FCSTD DOCUMENT  (FreeCAD 0.22R37100 (Git))
Label: composit_stand3_sleeve_model
License: All rights reserved
LicenseURL: http://en.wikipedia.org/wiki/All_rights_reserved
objects: App::Link×2, App::DocumentObjectGroup×1, PartDesign::CoordinateSystem×1, App::Part×1
note: 1 computed .brp shape members not serialized (recipe doc carries the construction recipe); baked Part::Feature solids carry a one-line shape summary decoded from their .brp
EXTERNAL_REF file=composit_stand3_sleeve_outer_model.FCStd obj=Local_CS
EXTERNAL_REF file=composit_stand3_sleeve_outer_model.FCStd obj=Body
EXTERNAL_REF file=composit_stand3_sleeve_outer_model.FCStd obj=Local_CS001
EXTERNAL_REF file=composit_stand3_sleeve_inner_model.FCStd obj=Local_CS
EXTERNAL_REF file=composit_stand3_sleeve_inner_model.FCStd obj=Body

FEATURE [App::DocumentObjectGroup] Parts
FEATURE [PartDesign::CoordinateSystem] LCS_Origin
  AttacherType = Attacher::AttachEngine3D
FEATURE [App::Link] sleeve_outer
  AttachedBy = #Local_CS
  AttachedTo = Parent Assembly#LCS_Origin
  LinkedObject = -> <external composit_stand3_sleeve_outer_model.FCStd>#Body
  SolverId = Asm4EE
  expr: Placement = LCS_Origin.Placement * AttachmentOffset * Unnamed#Local_CS.Placement ^ -1
FEATURE [App::Link] sleeve_inner
  AttachedBy = #Local_CS
  AttachedTo = sleeve_outer#Local_CS001
  LinkPlacement = pos=(0,2.3e-15,58.6519) rot=(1,0,0;3.14159rad)
  LinkedObject = -> <external composit_stand3_sleeve_inner_model.FCStd>#Body
  Placement = pos=(0,2.3e-15,58.6519) rot=(1,0,0;3.14159rad)
  SolverId = Asm4EE
  expr: Placement = sleeve_outer.Placement * Unnamed#Local_CS001.Placement * AttachmentOffset * composit_stand3_sleeve_inner_model#Local_CS.Placement ^ -1
FEATURE [App::Part] Assembly
  AssemblyType = Part::Link
  Group = -> [LCS_Origin,sleeve_outer,sleeve_inner]
  Origin = -> Origin
  Type = Assembly

RESOLVED EXTERNAL PARTS (link-assembly join: the EXTERNAL_REF files above that resolve inside this repo's crawl, each included once):
---- part composit_stand3_sleeve_inner_model.FCStd = doc fcstd_342576fd2858 ----
FCSTD DOCUMENT  (FreeCAD 1.1R38827 (Git))
Label: composit_stand3_sleeve_inner_model
License: All rights reserved
LicenseURL: http://en.wikipedia.org/wiki/All_rights_reserved
objects: PartDesign::SubShapeBinder×2, PartDesign::Body×2, PartDesign::Revolution×1, PartDesign::CoordinateSystem×1, Part::Feature×1, App::Link×1, Part::Cylinder×1, Part::FeaturePython×1, Part::MultiFuse×1, PartDesign::Boolean×1
note: 14 computed .brp shape members not serialized (recipe doc carries the construction recipe); baked Part::Feature solids carry a one-line shape summary decoded from their .brp
EXTERNAL_REF file=composit_stand3_sleeve_inner_main.FCStd obj=Sketch
EXTERNAL_REF file=composit_stand3_sleeve_inner_main.FCStd obj=PolarArray

FEATURE [PartDesign::SubShapeBinder] Binder
  BindCopyOnChange = 0
  BindMode = 0
  ClaimChildren = true
  Fuse = false
  MakeFace = true
  OffsetFill = false
  OffsetIntersection = false
  OffsetJoinType = 0
  OffsetOpenResult = false
  PartialLoad = false
  Placement = pos=(0,0,0) rot=(1,0,0;1.5708rad)
  Relative = false
  Support = -> [<external composit_stand3_sleeve_inner_main.FCStd>#Sketch]
  _Version = 2
FEATURE [PartDesign::SubShapeBinder] Binder001
  BindCopyOnChange = 0
  BindMode = 0
  ClaimChildren = true
  Context = -> Body [Binder001.]
  Fuse = false
  MakeFace = true
  OffsetFill = false
  OffsetIntersection = false
  OffsetJoinType = 0
  OffsetOpenResult = false
  PartialLoad = false
  Placement = pos=(0,0,0) rot=(1,0,0;1.5708rad)
  Relative = false
  Support = -> [Binder]
  _Version = 2
FEATURE [PartDesign::Revolution] Revolution
  Angle = 360
  Angle2 = 60
  Axis = (1e-16,1e-16,1)
  Base = (0,0,0)
  Placement = pos=(0,0,0) rot=(1,0,0;1.5708rad)
  Profile = -> Binder001 [Face1]
  ReferenceAxis = -> Z_Axis
  Reversed = true
  Suppressed = false
  Type = 0
FEATURE [PartDesign::CoordinateSystem] Local_CS
  AttacherType = Attacher::AttachEngine3D
  AttachmentOffset = pos=(0,0,8) rot=(0,0,1;0rad)
  AttachmentSupport = -> [XY_Plane]
  MapMode = 5
  Placement = pos=(0,0,8) rot=(0,0,1;0rad)
  expr: .AttachmentOffset.Base.z = <<composit_stand3_sleeve_inner_main>>#<<sleeve_inner_base_sketch>>.Constraints.base_height
FEATURE [Part::Feature] Body169  label="sleeve_inner002"
  shape: bbox 66 x 66 x 79 mm, 9 faces (baked)
FEATURE [App::Link] Link  label="PolarArray"
  LinkTransform = true
  LinkedObject = -> <external composit_stand3_sleeve_inner_main.FCStd>#PolarArray
FEATURE [Part::Cylinder] Cylinder
  Angle = 360
  AttacherType = Attacher::AttachEngine3D
  FirstAngle = 0
  Height = 20
  Placement = pos=(0,0,0) rot=(1,0,0;3.14159rad)
  Radius = 2
  SecondAngle = 0
FEATURE [Part::FeaturePython] Populate  label="Populate PolarArray with Cylinder"  # WARN: FeaturePython — macro-defined, semantics opaque (R4)
  Copying = 0
  ExposePlacement = false
  MarkerShape = 1
  MarkerSize = 0
  NumElements = 0
  Object = -> Cylinder
  OutputCompounding = 1
  PlacementsTo = -> Link
  Referencing = 0
  Type = lattice2PopulateCopies.LatticePopulateCopies
  isLattice = 0
FEATURE [PartDesign::Body] Body170  label="Body"
  AllowCompound = false
  Origin = -> Origin001
FEATURE [Part::MultiFuse] Fusion
  Shapes = -> [Populate]
FEATURE [PartDesign::Boolean] Boolean
  BaseFeature = -> Revolution
  Group = -> [Fusion]
  Suppressed = false
  Type = 1
  UsePlacement = true
FEATURE [PartDesign::Body] Body  label="sleeve_inner"
  AllowCompound = false
  Group = -> [Binder001,Revolution,Local_CS,Boolean]
  Origin = -> Origin
  Tip = -> Boolean
---- part composit_stand3_sleeve_outer_model.FCStd = doc fcstd_1b32ab60fdce ----
FCSTD DOCUMENT  (FreeCAD 1.1R38827 (Git))
Label: composit_stand3_sleeve_outer_model
License: All rights reserved
LicenseURL: http://en.wikipedia.org/wiki/All_rights_reserved
objects: PartDesign::SubShapeBinder×2, PartDesign::CoordinateSystem×2, PartDesign::Revolution×1, PartDesign::Body×1, Part::Feature×1
note: 9 computed .brp shape members not serialized (recipe doc carries the construction recipe); baked Part::Feature solids carry a one-line shape summary decoded from their .brp
EXTERNAL_REF file=composit_stand3_sleeve_outer_main.FCStd obj=Sketch

FEATURE [PartDesign::SubShapeBinder] Binder
  BindCopyOnChange = 0
  BindMode = 0
  ClaimChildren = true
  Fuse = false
  MakeFace = true
  OffsetFill = false
  OffsetIntersection = false
  OffsetJoinType = 0
  OffsetOpenResult = false
  PartialLoad = false
  Relative = false
  Support = -> [<external composit_stand3_sleeve_outer_main.FCStd>#Sketch]
  _Version = 2
FEATURE [PartDesign::SubShapeBinder] Binder001
  BindCopyOnChange = 0
  BindMode = 0
  ClaimChildren = true
  Context = -> Body [Binder001.]
  Fuse = false
  MakeFace = true
  OffsetFill = false
  OffsetIntersection = false
  OffsetJoinType = 0
  OffsetOpenResult = false
  PartialLoad = false
  Placement = pos=(0,0,0) rot=(1,0,0;1.5708rad)
  Relative = true
  Support = -> [Binder]
  _Version = 2
FEATURE [PartDesign::Revolution] Revolution
  Angle = 360
  Angle2 = 60
  Axis = (1e-16,1e-16,1)
  Base = (0,0,0)
  Placement = pos=(0,0,0) rot=(1,0,0;1.5708rad)
  Profile = -> Binder001 [Face1]
  ReferenceAxis = -> Z_Axis
  Reversed = true
  Suppressed = false
  Type = 0
FEATURE [PartDesign::CoordinateSystem] Local_CS  label="base_LCS"
  AttacherType = Attacher::AttachEngine3D
  AttachmentSupport = -> [XY_Plane]
  MapMode = 5
FEATURE [PartDesign::CoordinateSystem] Local_CS001
  AttacherType = Attacher::AttachEngine3D
  AttachmentOffset = pos=(0,0,67) rot=(1,0,0;3.14159rad)
  AttachmentSupport = -> [XY_Plane]
  MapMode = 5
  Placement = pos=(0,0,67) rot=(1,0,0;3.14159rad)
  expr: .AttachmentOffset.Base.z = <<composit_stand3_sleeve_outer_main>>#<<sleeve_outer_base_sketch>>.Constraints.height
FEATURE [PartDesign::Body] Body  label="sleeve_outer"
  AllowCompound = false
  Group = -> [Binder001,Revolution,Local_CS,Local_CS001]
  Origin = -> Origin
  Tip = -> Revolution
FEATURE [Part::Feature] Body170  label="sleeve_outer002"
  shape: bbox 70.5 x 70.5 x 67 mm, 9 faces (baked)
